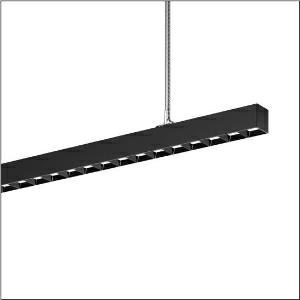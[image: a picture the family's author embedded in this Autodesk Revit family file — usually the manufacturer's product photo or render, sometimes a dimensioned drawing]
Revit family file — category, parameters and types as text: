
# Revit family: silica_r__21_51mx31tctdb_123f
name_source: partatom
category: Lighting Fixtures
units: mm (PartAtom-declared; Revit-internal decimal feet)

## family parameters
Cut with Voids When Loaded = No
Host = Face
Light Source = No
Part Type = Normal
Room Calculation Point = No
Round Connector Dimension = Use Diameter
Shared = No

## types (1)
- --- (1 x LED, 15550 lm, 133.9 W, 6500K)
    Apparent Load = 134 VA
    CIE Flux Codes = 85 99 100 60 100
    Color Rendering = 80
    Color Temperature = 6500K
    Default Elevation = 1800 mm
    Description = Silica® 21, office luminaire, primary light control with darklight reflector, of PMMA, black, CAT 2 (L<= 3000cd/m²), light emission: direct/indirect distribution, primary light characteristic: symmetric, installation type: suspended mounting, LED, rated luminous flux: 15.550lm, luminous efficacy: 111lm/W, light colour: 8tw, colour temperature: 2700..6500K, control gear: ECG DALI, with terminal, 3+2-pole, max. 2.5mm², mains connection: 220..240V, AC, 50/60Hz, rated input power: 140.6W, luminaire housing, of aluminium, jet black (RAL 9005), length: 3.004mm, width: 53mm, height: 53mm, protection rating (complete): IP20, insulation class (complete): insulation class I (protective earthing), certification: CE, permissible operating ambient temperature: 0..+35°C, standard: EN 50419, packaging unit: 1 piece
    Height = 53 mm
    Lamp = 1 x LED
    Lamp Light Flux = 15550 lm
    Lamp Power = 133.9 W
    Lamp count = 1
    Length = 3004 mm
    Luminous efficacy = 116 lm/W
    Manufacturer = Siteco
    ModVariant = No
    Model = 51MX31TCTDB
    Mounting Place = Ceiling
    Mounting Type = Pendant
    Number of Poles = 1
    OnlyDefault = Yes
    Power Factor = 1
    Product Name = Silica® 21
    Product group = office luminaire | ceiling pendant
    ProductGroupID = 902
    Protection Class = Protection class I
    Protection Degree = IP 20
    RLX_Detail_Level = 1
    RLX_Emergency_Light_Flux = 0 lm
    RLX_Emergency_Type = 0
    RLX_Emergency_Type_DB = No
    RlxData = <blob elided: 62637 chars, md5=d19bc6cd>
    Socket = socket
    Standby Power = 0 W
    System Light Flux = 15550 lm
    System Power = 134 W
    Type Comments = individual setting
    Type Image = l_1335852.jpg
    URL = http://relux.com
    VarID = @adj_109681
    Voltage = 0 V
    Weight = 0.00 kg
    Width = 53 mm

## geometry (parser evidence)
native form markers: Blend x4, Sweep x11
no freeform markers — native parametric forms only
